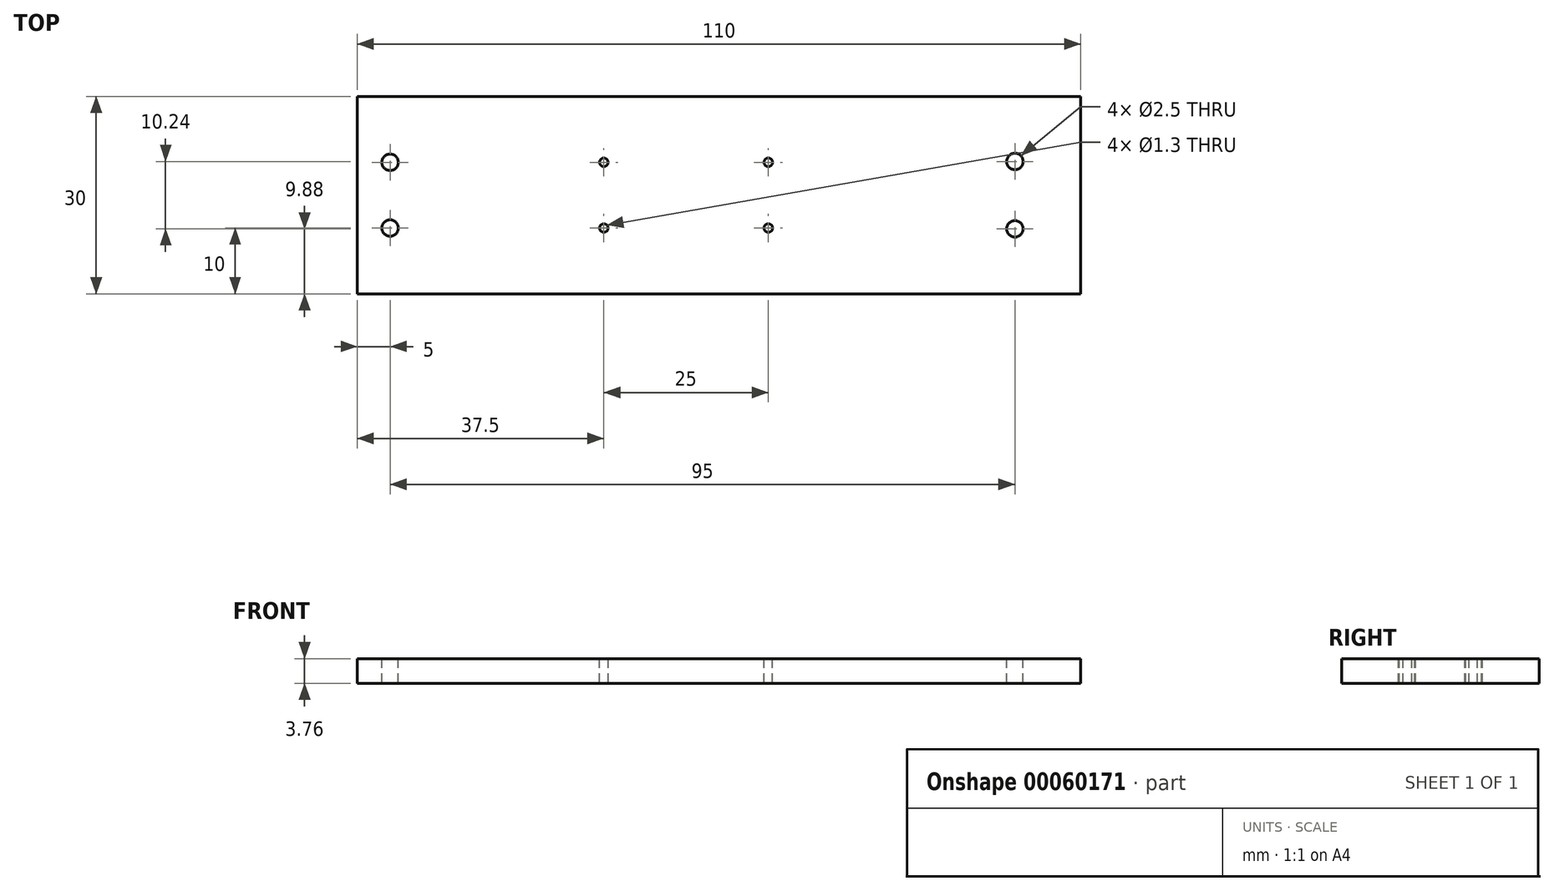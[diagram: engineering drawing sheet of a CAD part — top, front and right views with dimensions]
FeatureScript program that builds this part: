
annotation { "Feature Type Name" : "Feature", "Feature Type Description" : "" }
export const myFeature = defineFeature(function(context is Context, id is Id, definition is map)
    precondition{}
    {
        {
            var Q0;
            Q0=qCreatedBy(makeId("Right.planeOp"),FACE);
            var sketch = newSketch(context, id + "F0", { "sketchPlane" : qUnion([Q0])});
            skLineSegment(sketch, "E0.rect.bottom", {"start": v(15, 1.88) * mm, "end": v(-15, 1.88) * mm});
            skLineSegment(sketch, "E0.rect.top", {"start": v(15, -1.87) * mm, "end": v(-15, -1.87) * mm});
            skLineSegment(sketch, "E0.rect.left", {"start": v(15, 1.88) * mm, "end": v(15, -1.88) * mm});
            skLineSegment(sketch, "E0.rect.right", {"start": v(-15, 1.88) * mm, "end": v(-15, -1.87) * mm});
            skPoint(sketch, "E0.rect.middle", {"position": v(0, 0) * mm});
            skSolve(sketch);
        }
        {
            var Q0;
            Q0=qSketchRegion(id+"F0",true);
            extrude(context, id + "F1", {"entities" : qUnion([Q0]), "depth" : 110 * mm, "symmetric" : true});
        }
        {
            var Q0;
            Q0=makeQuery(id+"F1.opExtrude","SWEPT_FACE",FACE,{"disambiguationData":[OSD([sQuery(id+"F0.wireOp",EDGE,"E0.rect.bottom")])]});
            var sketch = newSketch(context, id + "F2", { "sketchPlane" : qUnion([Q0])});
            skCircle(sketch, "E1", {"center": v(-50, 5) * mm, "radius": 1.25 * mm});
            skCircle(sketch, "E2", {"center": v(45, -5.12) * mm, "radius": 1.25 * mm});
            skCircle(sketch, "E3", {"center": v(45, 5.12) * mm, "radius": 1.25 * mm});
            skCircle(sketch, "E4", {"center": v(-50, -5) * mm, "radius": 1.25 * mm});
            skSolve(sketch);
        }
        {
            var Q0;
            Q0=qSketchRegion(id+"F2",true);
            extrude(context, id + "F3", {"entities" : qUnion([Q0]), "operationType" : NewBodyOperationType.REMOVE, "endBound" : BoundingType.THROUGH_ALL, "oppositeDirection" : true, "depth" : 25 * mm});
        }
        {
            var Q0;
            Q0=makeQuery(id+"F1.opExtrude","SWEPT_FACE",FACE,{"disambiguationData":[OSD([sQuery(id+"F0.wireOp",EDGE,"E0.rect.bottom")])]});
            var sketch = newSketch(context, id + "F4", { "sketchPlane" : qUnion([Q0])});
            skCircle(sketch, "E5", {"center": v(-17.5, 5) * mm, "radius": 0.65 * mm});
            skCircle(sketch, "E6", {"center": v(-17.5, -5) * mm, "radius": 0.65 * mm});
            skCircle(sketch, "E7", {"center": v(7.5, 5) * mm, "radius": 0.65 * mm});
            skCircle(sketch, "E8", {"center": v(7.5, -5) * mm, "radius": 0.65 * mm});
            skSolve(sketch);
        }
        {
            var Q0;
            Q0 = qSketchRegion(id + "F4", true);
            extrude(context, id + "F5", {"entities" : qUnion([Q0]), "operationType" : NewBodyOperationType.REMOVE, "endBound" : BoundingType.THROUGH_ALL, "oppositeDirection" : true, "depth" : 25 * mm});
        }
    });
